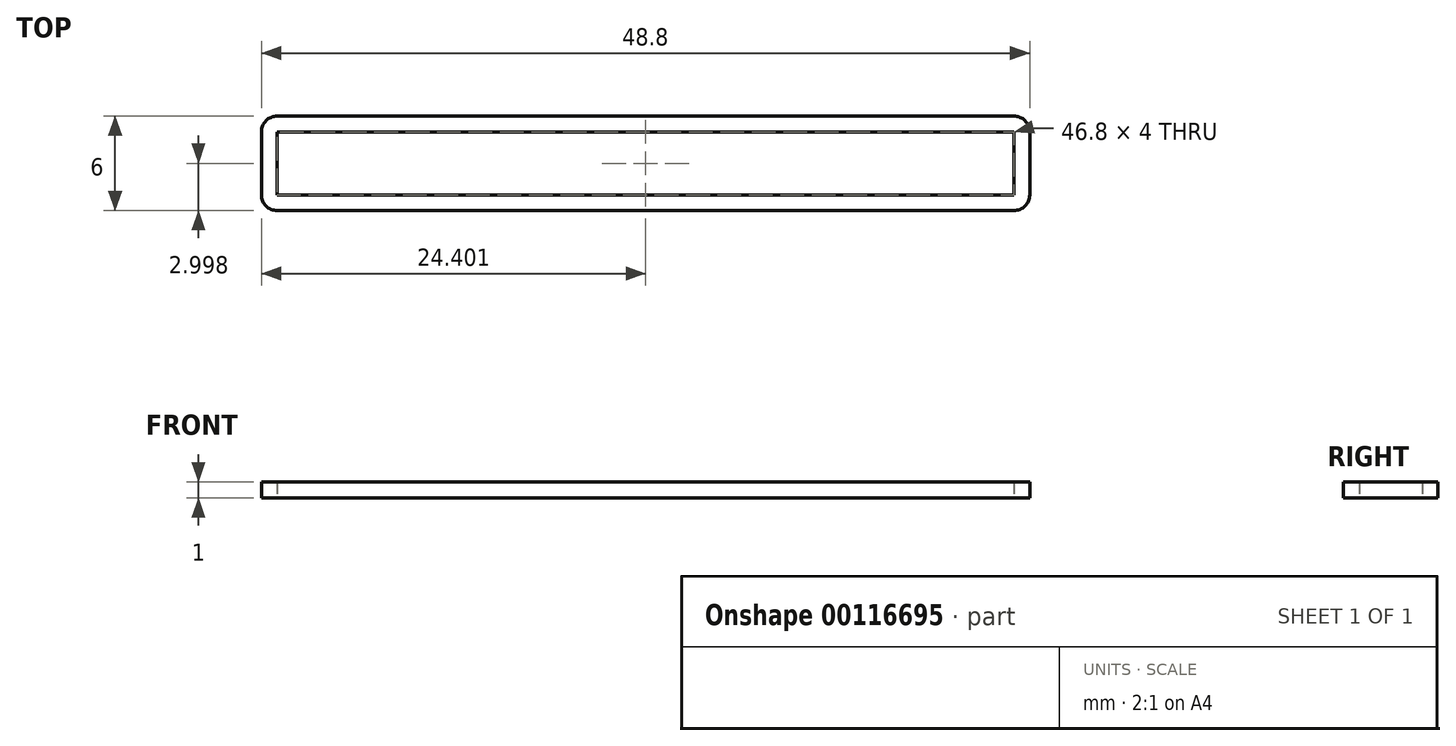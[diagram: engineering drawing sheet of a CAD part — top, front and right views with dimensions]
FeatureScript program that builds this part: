
annotation { "Feature Type Name" : "Feature", "Feature Type Description" : "" }
export const myFeature = defineFeature(function(context is Context, id is Id, definition is map)
    precondition{}
    {
        {
            var Q0;
            Q0=qCreatedBy(makeId("Top.planeOp"),FACE);
            var sketch = newSketch(context, id + "F0", { "sketchPlane" : qUnion([Q0])});
            skLineSegment(sketch, "E0.bottom", {"start": v(-51.53, 31.13) * mm, "end": v(-4.73, 31.13) * mm});
            skLineSegment(sketch, "E0.top", {"start": v(-51.53, 27.13) * mm, "end": v(-4.73, 27.13) * mm});
            skLineSegment(sketch, "E0.left", {"start": v(-51.53, 31.13) * mm, "end": v(-51.53, 27.13) * mm});
            skLineSegment(sketch, "E0.right", {"start": v(-4.73, 31.13) * mm, "end": v(-4.73, 27.13) * mm});
            skLineSegment(sketch, "E1.0", {"start": v(-52.53, 32.13) * mm, "end": v(-3.73, 32.13) * mm});
            skLineSegment(sketch, "E1.1", {"start": v(-52.53, 32.13) * mm, "end": v(-52.53, 26.13) * mm});
            skLineSegment(sketch, "E1.2", {"start": v(-52.53, 26.13) * mm, "end": v(-3.73, 26.13) * mm});
            skLineSegment(sketch, "E1.3", {"start": v(-3.73, 32.13) * mm, "end": v(-3.73, 26.13) * mm});
            skSolve(sketch);
        }
        {
            var Q0;
            Q0 = qSketchRegion(id + "F0", true);
            extrude(context, id + "F1", {"entities" : qUnion([Q0]), "depth" : 1 * mm});
        }
        {
            var Q0;
            Q0=makeQuery(id+"F1.opExtrude","SWEPT_EDGE",EDGE,{"disambiguationData":[OSD([sQuery(id+"F0.wireOp",EDGE,"E1.2"),sQuery(id+"F0.wireOp",EDGE,"E1.3")])]});
            var Q1;
            Q1=makeQuery(id+"F1.opExtrude","SWEPT_EDGE",EDGE,{"disambiguationData":[OSD([sQuery(id+"F0.wireOp",EDGE,"E1.0"),sQuery(id+"F0.wireOp",EDGE,"E1.3")])]});
            var Q2;
            Q2=makeQuery(id+"F1.opExtrude","SWEPT_EDGE",EDGE,{"disambiguationData":[OSD([sQuery(id+"F0.wireOp",EDGE,"E1.1"),sQuery(id+"F0.wireOp",EDGE,"E1.2")])]});
            var Q3;
            Q3=makeQuery(id+"F1.opExtrude","SWEPT_EDGE",EDGE,{"disambiguationData":[OSD([sQuery(id+"F0.wireOp",EDGE,"E1.0"),sQuery(id+"F0.wireOp",EDGE,"E1.1")])]});
            fillet(context, id + "F2", {"entities" : qUnion([Q0, Q1, Q2, Q3]), "radius" : 1 * mm, "tangentPropagation" : true, "allowEdgeOverflow" : false});
        }
    });
